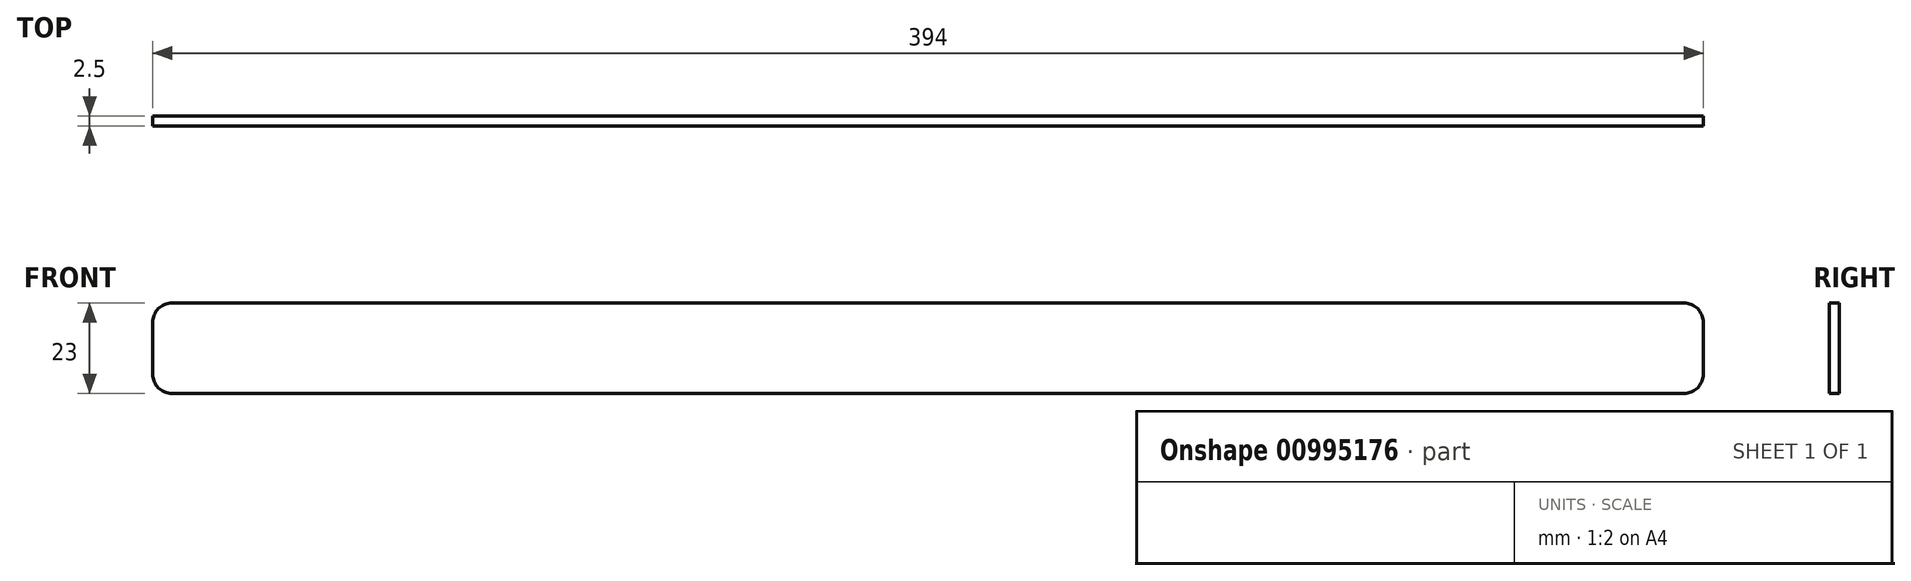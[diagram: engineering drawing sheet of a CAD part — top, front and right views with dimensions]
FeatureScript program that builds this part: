
annotation { "Feature Type Name" : "Feature", "Feature Type Description" : "" }
export const myFeature = defineFeature(function(context is Context, id is Id, definition is map)
    precondition{}
    {
        {
            var Q0;
            Q0=qCreatedBy(makeId("Front.planeOp"),FACE);
            var sketch = newSketch(context, id + "F0", { "sketchPlane" : qUnion([Q0])});
            skLineSegment(sketch, "E0.bottom", {"start": v(-197, 11.5) * mm, "end": v(197, 11.5) * mm});
            skLineSegment(sketch, "E0.top", {"start": v(-197, -11.5) * mm, "end": v(197, -11.5) * mm});
            skLineSegment(sketch, "E0.left", {"start": v(-197, 11.5) * mm, "end": v(-197, -11.5) * mm});
            skLineSegment(sketch, "E0.right", {"start": v(197, 11.5) * mm, "end": v(197, -11.5) * mm});
            skPoint(sketch, "E0.middle", {"position": v(0, 0) * mm});
            skSolve(sketch);
        }
        {
            var Q0;
            Q0=makeQuery(id+"F0.imprint","IMPRINT",FACE,{"disambiguationData":[TD([[makeQuery(id+"F0.imprint","IMPRINT",EDGE,{"derivedFrom":sQuery(id+"F0.wireOp",EDGE,"E0.bottom")}),-1.0]])]});
            extrude(context, id + "F1", {"entities" : qUnion([Q0]), "depth" : 2.5 * mm, "offsetDistance" : 25 * mm, "symmetric" : true});
        }
        {
            var Q0;
            Q0=makeQuery(id+"F1.opExtrude","SWEPT_EDGE",EDGE,{"disambiguationData":[OSD([sQuery(id+"F0.wireOp",EDGE,"E0.bottom"),sQuery(id+"F0.wireOp",EDGE,"E0.left")])]});
            var Q1;
            Q1=makeQuery(id+"F1.opExtrude","SWEPT_EDGE",EDGE,{"disambiguationData":[OSD([sQuery(id+"F0.wireOp",EDGE,"E0.top"),sQuery(id+"F0.wireOp",EDGE,"E0.left")])]});
            var Q2;
            Q2=makeQuery(id+"F1.opExtrude","SWEPT_EDGE",EDGE,{"disambiguationData":[OSD([sQuery(id+"F0.wireOp",EDGE,"E0.bottom"),sQuery(id+"F0.wireOp",EDGE,"E0.right")])]});
            var Q3;
            Q3=makeQuery(id+"F1.opExtrude","SWEPT_EDGE",EDGE,{"disambiguationData":[OSD([sQuery(id+"F0.wireOp",EDGE,"E0.top"),sQuery(id+"F0.wireOp",EDGE,"E0.right")])]});
            fillet(context, id + "F2", {"entities" : qUnion([Q0, Q1, Q2, Q3]), "radius" : 5 * mm, "tangentPropagation" : true, "allowEdgeOverflow" : false});
        }
    });
